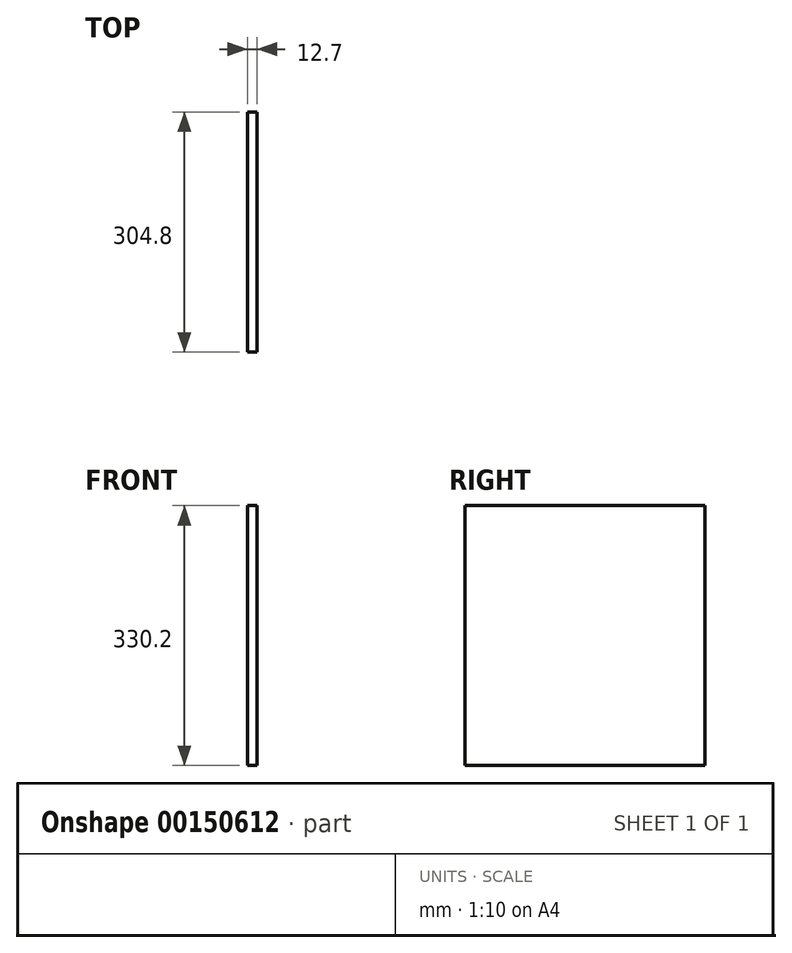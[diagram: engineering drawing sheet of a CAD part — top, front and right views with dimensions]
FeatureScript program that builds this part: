
annotation { "Feature Type Name" : "Feature", "Feature Type Description" : "" }
export const myFeature = defineFeature(function(context is Context, id is Id, definition is map)
    precondition{}
    {
        {
            var Q0;
            Q0=qCreatedBy(makeId("Front.planeOp"),FACE);
            var sketch = newSketch(context, id + "F0", { "sketchPlane" : qUnion([Q0])});
            skLineSegment(sketch, "E0.bottom", {"start": v(-26.85, -29.57) * mm, "end": v(-14.15, -29.57) * mm});
            skLineSegment(sketch, "E0.top", {"start": v(-26.85, 300.63) * mm, "end": v(-14.15, 300.63) * mm});
            skLineSegment(sketch, "E0.left", {"start": v(-26.85, -29.57) * mm, "end": v(-26.85, 300.63) * mm});
            skLineSegment(sketch, "E0.right", {"start": v(-14.15, -29.57) * mm, "end": v(-14.15, 300.63) * mm});
            skSolve(sketch);
        }
        {
            var Q0;
            Q0 = qSketchRegion(id + "F0", true);
            extrude(context, id + "F1", {"entities" : qUnion([Q0]), "depth" : 304.8 * mm});
        }
    });
